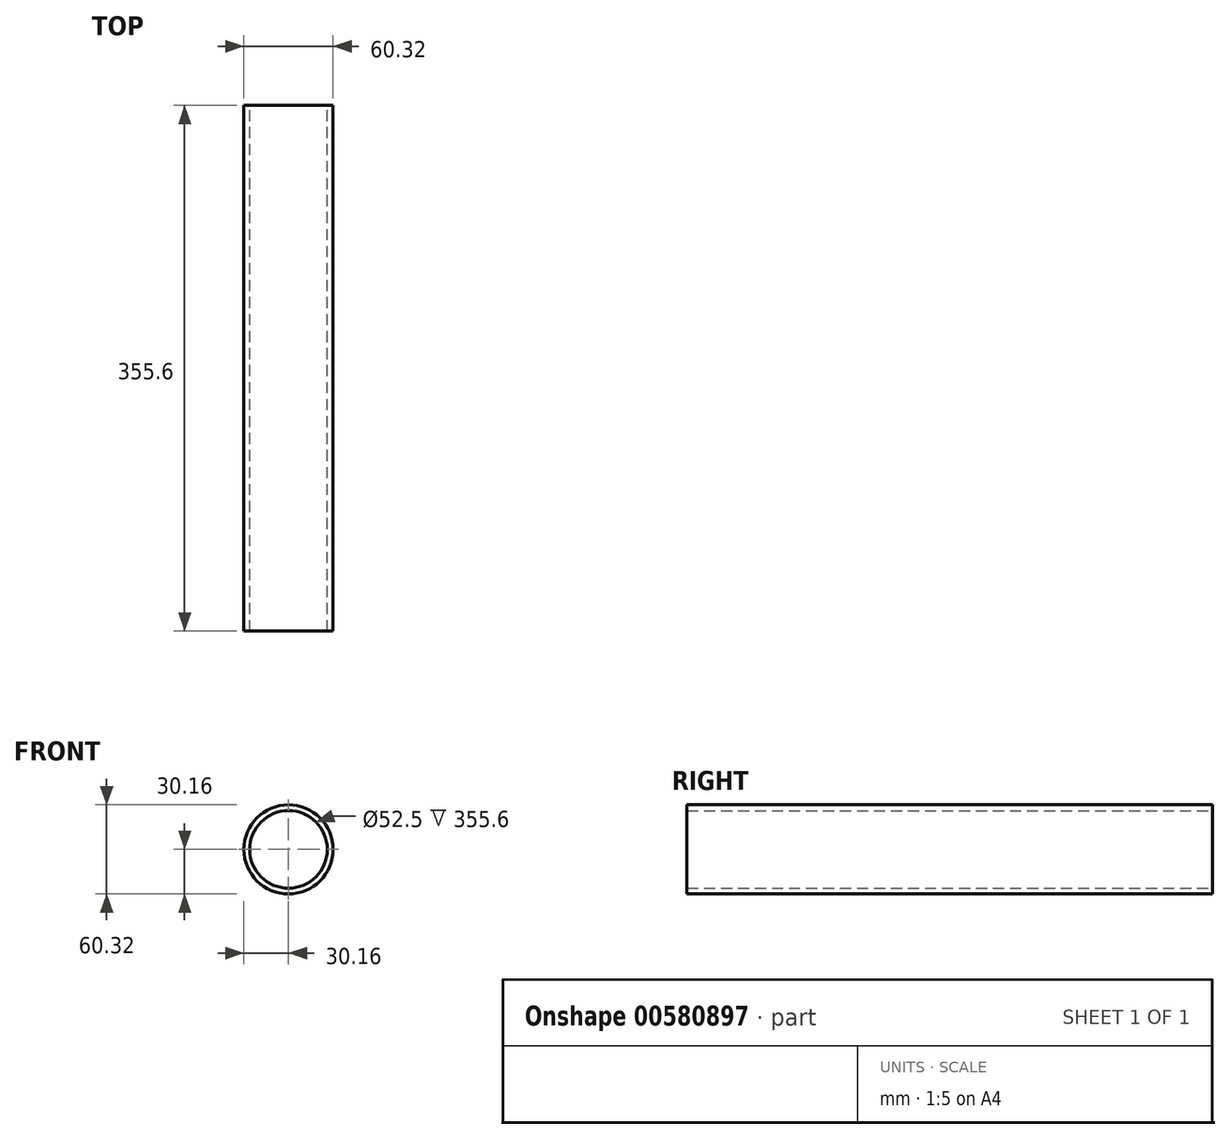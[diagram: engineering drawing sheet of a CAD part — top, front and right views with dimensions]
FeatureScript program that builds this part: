
annotation { "Feature Type Name" : "Feature", "Feature Type Description" : "" }
export const myFeature = defineFeature(function(context is Context, id is Id, definition is map)
    precondition{}
    {
        {
            var Q0;
            Q0=qCreatedBy(makeId("Front.planeOp"),FACE);
            var sketch = newSketch(context, id + "F0", { "sketchPlane" : qUnion([Q0])});
            skCircle(sketch, "E0", {"center": v(0, 0) * mm, "radius": 30.16 * mm});
            skCircle(sketch, "E1.0", {"center": v(0, 0) * mm, "radius": 26.25 * mm});
            skSolve(sketch);
        }
        {
            var Q0;
            Q0 = qSketchRegion(id + "F0", true);
            extrude(context, id + "F1", {"entities" : qUnion([Q0]), "endBound" : BoundingType.SYMMETRIC, "depth" : 355.6 * mm, "offsetDistance" : 25 * mm});
        }
    });
